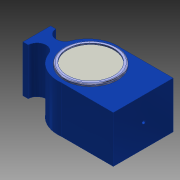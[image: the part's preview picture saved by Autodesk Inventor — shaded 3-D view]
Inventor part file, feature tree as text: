
AUTODESK INVENTOR PART (.ipt)
format: ipt  version: 2015 (Build 190159000, 159)  size: 136,704 bytes
history: native  units: in
note: dims shown in document units (in); Inventor stores cm internally (conversion verified against a paired STEP export)
features: extrude x3, sketch x2, hole x1, fillet x1
ambient origin geometry x8: Origin, YZ Plane, XZ Plane, XY Plane, X Axis, Y Axis, Z Axis, Center Point
bodies: Solid1 (feature_tree)
feature tree (7):
  extrude  "Extrusion1"  Depth=4.0in
  hole  "Hole1"  [1 undecoded]
  sketch  "Sketch2"  dims[d3=1.75in d4=0.0in d5=1.0in d6=1.0in d7=0.125in d8=0.75in d9=0.375in d10=0.25in d11=0.5635in d12=1.0in d13=0.8108in d14=2.0in d15=1.0in d18=1.75in d19=0.1in d20=0.0in d21=0.05in d22=0.0in d23=0.05in]
  extrude  "Extrusion3"  Depth=0.05in
  extrude  "Extrusion4"  Depth=1.0in
  fillet  "Fillet1"  Radius=1.75in
  sketch  "Sketch1"  dims[d1=2.25in d2=4.0in]
note: 1 required parameter value undecoded (feature->parameter linkage not recoverable at this tier; creation-order binding heuristic only, values carry confidence <= 0.55)
